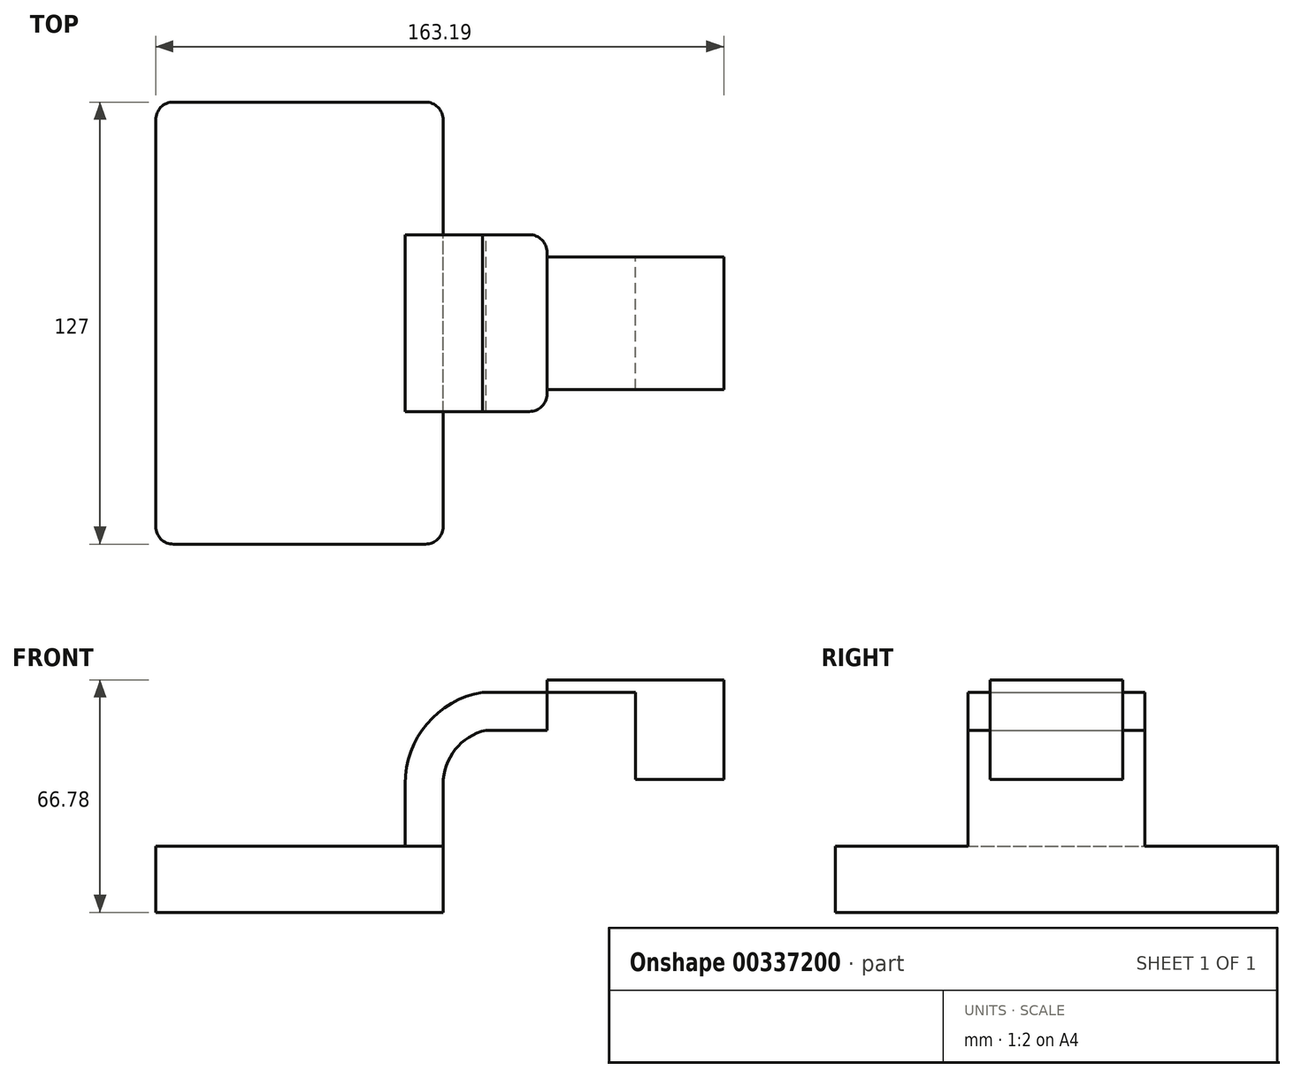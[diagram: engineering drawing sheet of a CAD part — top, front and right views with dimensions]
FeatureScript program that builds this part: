
annotation { "Feature Type Name" : "Feature", "Feature Type Description" : "" }
export const myFeature = defineFeature(function(context is Context, id is Id, definition is map)
    precondition{}
    {
        {
            var Q0;
            Q0=qCreatedBy(makeId("Front.planeOp"),FACE);
            var sketch = newSketch(context, id + "F0", { "sketchPlane" : qUnion([Q0])});
            skLineSegment(sketch, "E0.bottom", {"start": v(-41.28, 9.52) * mm, "end": v(41.27, 9.53) * mm});
            skLineSegment(sketch, "E0.top", {"start": v(-41.28, -9.53) * mm, "end": v(41.28, -9.53) * mm});
            skLineSegment(sketch, "E0.left", {"start": v(-41.28, 9.52) * mm, "end": v(-41.28, -9.53) * mm});
            skLineSegment(sketch, "E0.right", {"start": v(41.27, 9.53) * mm, "end": v(41.28, -9.52) * mm});
            skPoint(sketch, "E0.middle", {"position": v(0, 0) * mm});
            skLineSegment(sketch, "E1.bottom", {"start": v(71.12, 57.25) * mm, "end": v(121.92, 57.25) * mm});
            skLineSegment(sketch, "E1.top", {"start": v(71.12, 28.67) * mm, "end": v(121.92, 28.67) * mm});
            skLineSegment(sketch, "E1.left", {"start": v(71.12, 57.25) * mm, "end": v(71.12, 28.67) * mm});
            skLineSegment(sketch, "E1.right", {"start": v(121.92, 57.25) * mm, "end": v(121.92, 28.67) * mm});
            skPoint(sketch, "E1.middle", {"position": v(96.52, 42.96) * mm});
            skLineSegment(sketch, "E2", {"start": v(41.27, 9.53) * mm, "end": v(41.27, 27.32) * mm});
            skArc(sketch, "E3", {"start": v(41.27, 27.32) * mm, "mid": v(44.74, 37.22) * mm, "end": v(53.63, 42.8) * mm});
            skPoint(sketch, "E4.endSnap0", {"position": v(71.12, 42.96) * mm});
            skLineSegment(sketch, "E5", {"start": v(53.63, 42.8) * mm, "end": v(85.73, 42.8) * mm});
            skLineSegment(sketch, "E6.0", {"start": v(52.57, 53.72) * mm, "end": v(85.73, 53.72) * mm});
            skArc(sketch, "E6.1", {"start": v(30.35, 27.32) * mm, "mid": v(36.64, 44.57) * mm, "end": v(52.57, 53.72) * mm});
            skLineSegment(sketch, "E6.2", {"start": v(30.35, 9.53) * mm, "end": v(30.35, 27.32) * mm});
            skFitSpline(sketch, "E7", {"points": [v(-41.28, 9.52) * mm, v(52.57, 53.72) * mm], "startDerivative": vector(62.89, 95.36) * mm, "endDerivative": vector(134.98, -8.22) * mm});
            skLineSegment(sketch, "E8", {"start": v(81.68, 42.8) * mm, "end": v(96.52, 42.96) * mm});
            skLineSegment(sketch, "E9", {"start": v(83.48, 53.72) * mm, "end": v(96.52, 53.72) * mm});
            skLineSegment(sketch, "E10", {"start": v(96.52, 57.25) * mm, "end": v(96.52, 28.67) * mm});
            skSolve(sketch);
        }
        {
            var Q0;
            Q0=makeQuery(id+"F0.imprint","IMPRINT",FACE,{"disambiguationData":[TD([[makeQuery(id+"F0.imprint","IMPRINT",EDGE,{"derivedFrom":sQuery(id+"F0.wireOp",EDGE,"E0.top")}),1.0]])]});
            extrude(context, id + "F1", {"entities" : qUnion([Q0]), "endBound" : BoundingType.SYMMETRIC, "depth" : 127 * mm});
        }
        {
            var Q0;
            {var subQ1=sQuery(id+"F0.wireOp",EDGE,"E2");Q0=makeQuery(id+"F0.imprint","IMPRINT",FACE,{"disambiguationData":[TD([[makeQuery(id+"F0.imprint","IMPRINT",EDGE,{"derivedFrom":subQ1}),1.0]])]});}
            extrude(context, id + "F2", {"entities" : qUnion([Q0]), "operationType" : NewBodyOperationType.ADD, "endBound" : BoundingType.SYMMETRIC, "depth" : 50.8 * mm});
        }
        {
            var Q0;
            Q0=makeQuery(id+"F0.imprint","IMPRINT",FACE,{"disambiguationData":[TD([[makeQuery(id+"F0.imprint","IMPRINT",EDGE,{"derivedFrom":sQuery(id+"F0.wireOp",EDGE,"E6.1")}),1.0]])]});
            extrude(context, id + "F3", {"entities" : qUnion([Q0]), "operationType" : NewBodyOperationType.ADD, "endBound" : BoundingType.SYMMETRIC, "depth" : 25.4 * mm});
        }
        {
            var Q0;
            {var subQ3=sQuery(id+"F0.wireOp",EDGE,"E1.bottom");Q0=makeQuery(id+"F0.imprint","IMPRINT",FACE,{"disambiguationData":[TD([[makeQuery(id+"F0.imprint","IMPRINT",EDGE,{"derivedFrom":subQ3}),-1.0]])]});}
            extrude(context, id + "F4", {"entities" : qUnion([Q0]), "operationType" : NewBodyOperationType.ADD, "endBound" : BoundingType.SYMMETRIC, "depth" : 38.1 * mm});
        }
        {
            var Q0;
            Q0=makeQuery(id+"F1.opExtrude","CAP_EDGE",EDGE,{"disambiguationData":[OSD([sQuery(id+"F0.wireOp",EDGE,"E0.left")])],"isStart":false});
            var Q1;
            Q1=makeQuery(id+"F1.opExtrude","CAP_EDGE",EDGE,{"disambiguationData":[OSD([sQuery(id+"F0.wireOp",EDGE,"E0.right")])],"isStart":false});
            var Q2;
            Q2=makeQuery(id+"F1.opExtrude","CAP_EDGE",EDGE,{"disambiguationData":[OSD([sQuery(id+"F0.wireOp",EDGE,"E0.left")])],"isStart":true});
            var Q3;
            Q3=makeQuery(id+"F1.opExtrude","CAP_EDGE",EDGE,{"disambiguationData":[OSD([sQuery(id+"F0.wireOp",EDGE,"E0.right")])],"isStart":true});
            var Q4;
            Q4=makeQuery(id+"F2.opExtrude","CAP_EDGE",EDGE,{"disambiguationData":[OSD([sQuery(id+"F0.wireOp",EDGE,"E1.left")])],"isStart":true});
            var Q5;
            Q5=makeQuery(id+"F2.opExtrude","CAP_EDGE",EDGE,{"disambiguationData":[OSD([sQuery(id+"F0.wireOp",EDGE,"E1.left")])],"isStart":false});
            fillet(context, id + "F5", {"entities" : qUnion([Q0, Q1, Q2, Q3, Q4, Q5]), "radius" : 5.08 * mm, "tangentPropagation" : true, "allowEdgeOverflow" : false});
        }
    });
